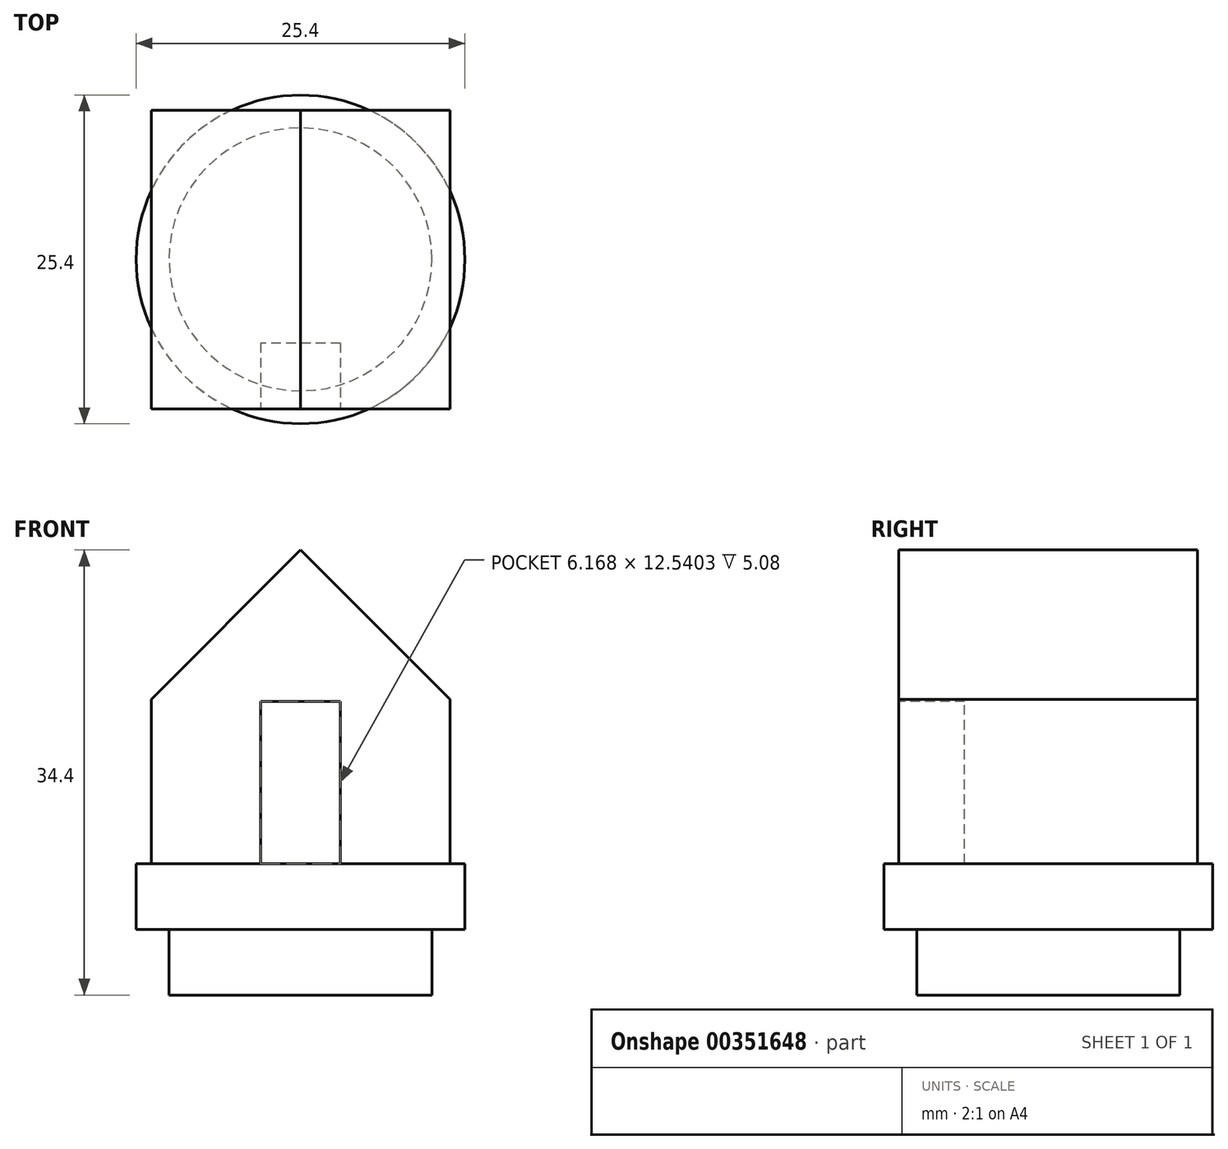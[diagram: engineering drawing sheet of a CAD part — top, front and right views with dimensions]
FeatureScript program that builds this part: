
annotation { "Feature Type Name" : "Feature", "Feature Type Description" : "" }
export const myFeature = defineFeature(function(context is Context, id is Id, definition is map)
    precondition{}
    {
        {
            var Q0;
            Q0=qCreatedBy(makeId("Top.planeOp"),FACE);
            var sketch = newSketch(context, id + "F0", { "sketchPlane" : qUnion([Q0])});
            skCircle(sketch, "E0", {"center": v(0, 0) * mm, "radius": 10.16 * mm});
            skSolve(sketch);
        }
        {
            var Q0;
            Q0=makeQuery(id+"F0.imprint","IMPRINT",FACE,{"disambiguationData":[TD([[makeQuery(id+"F0.imprint","IMPRINT",EDGE,{"derivedFrom":sQuery(id+"F0.wireOp",EDGE,"E0")}),1.0]])]});
            extrude(context, id + "F1", {"entities" : qUnion([Q0]), "depth" : 5.08 * mm});
        }
        {
            var Q0;
            Q0=makeQuery(id+"F1.opExtrude","CAP_FACE",FACE,{"disambiguationData":[OSD([sQuery(id+"F0.wireOp",EDGE,"E0")])],"isStart":false});
            var sketch = newSketch(context, id + "F2", { "sketchPlane" : qUnion([Q0])});
            skCircle(sketch, "E1", {"center": v(0, 0) * mm, "radius": 12.7 * mm});
            skSolve(sketch);
        }
        {
            var Q0;
            Q0=makeQuery(id+"F2.imprint","IMPRINT",FACE,{"disambiguationData":[TD([[makeQuery(id+"F2.imprint","IMPRINT",EDGE,{"derivedFrom":sQuery(id+"F2.wireOp",EDGE,"E1")}),1.0]])]});
            var Q1;
            Q1=makeQuery(id+"F2.imprint","IMPRINT",FACE,{"disambiguationData":[TD([[makeQuery(id+"F2.imprint","IMPRINT",EDGE,{"derivedFrom":makeQuery(id+"F1.opExtrude","CAP_EDGE",EDGE,{"disambiguationData":[OSD([sQuery(id+"F0.wireOp",EDGE,"E0")])],"isStart":false})}),1.0]])]});
            extrude(context, id + "F3", {"entities" : qUnion([Q0, Q1]), "operationType" : NewBodyOperationType.ADD, "depth" : 5.08 * mm});
        }
        {
            var Q0;
            Q0=makeQuery(id+"F3.opExtrude","CAP_FACE",FACE,{"disambiguationData":[OSD([sQuery(id+"F2.wireOp",EDGE,"E1")])],"isStart":false});
            var sketch = newSketch(context, id + "F4", { "sketchPlane" : qUnion([Q0])});
            skLineSegment(sketch, "E2", {"start": v(0, -11.54) * mm, "end": v(0, -12.7) * mm});
            skLineSegment(sketch, "E3", {"start": v(12.7, 0) * mm, "end": v(11.54, 0) * mm});
            skLineSegment(sketch, "E4", {"start": v(8.98, -8.98) * mm, "end": v(11.54, -11.54) * mm});
            skLineSegment(sketch, "E5.bottom", {"start": v(11.54, -11.54) * mm, "end": v(-11.54, -11.54) * mm});
            skLineSegment(sketch, "E5.top", {"start": v(11.54, 11.54) * mm, "end": v(-11.54, 11.54) * mm});
            skLineSegment(sketch, "E5.left", {"start": v(11.54, -11.54) * mm, "end": v(11.54, 11.54) * mm});
            skLineSegment(sketch, "E5.right", {"start": v(-11.54, -11.54) * mm, "end": v(-11.54, 11.54) * mm});
            skPoint(sketch, "E5.middle", {"position": v(0, 0) * mm});
            skSolve(sketch);
        }
        {
            var Q0;
            {var subQ0=sQuery(id+"F4.wireOp",EDGE,"E5.bottom");var subQ13=makeQuery(id+"F4.imprint","INTERSECT",VERTEX,{"derivedFrom":[sQuery(id+"F4.wireOp",EDGE,"E2"),subQ0]});Q0=makeQuery(id+"F4.imprint","IMPRINT",FACE,{"disambiguationData":[TD([[makeQuery(id+"F4.imprint","IMPRINT",EDGE,{"disambiguationData":[TD([[subQ13,1.0]])],"derivedFrom":subQ0}),-1.0]])]});}
            var Q1;
            {var subQ0=sQuery(id+"F4.wireOp",EDGE,"E5.right");var subQ1=sQuery(id+"F4.wireOp",EDGE,"E5.bottom");var subQ2=makeQuery(id+"F4.imprint","INTERSECT",VERTEX,{"derivedFrom":[subQ1,subQ0]});Q1=makeQuery(id+"F4.imprint","IMPRINT",FACE,{"disambiguationData":[TD([[makeQuery(id+"F4.imprint","IMPRINT",EDGE,{"disambiguationData":[TD([[subQ2,1.0]])],"derivedFrom":subQ1}),-1.0]])]});}
            var Q2;
            {var subQ0=sQuery(id+"F4.wireOp",EDGE,"E4");Q2=makeQuery(id+"F4.imprint","IMPRINT",FACE,{"disambiguationData":[TD([[makeQuery(id+"F4.imprint","IMPRINT",EDGE,{"derivedFrom":subQ0}),1.0]])]});}
            var Q3;
            {var subQ0=sQuery(id+"F4.wireOp",EDGE,"E4");Q3=makeQuery(id+"F4.imprint","IMPRINT",FACE,{"disambiguationData":[TD([[makeQuery(id+"F4.imprint","IMPRINT",EDGE,{"derivedFrom":subQ0}),-1.0]])]});}
            var Q4;
            {var subQ0=sQuery(id+"F4.wireOp",EDGE,"E5.right");var subQ1=sQuery(id+"F4.wireOp",EDGE,"E5.top");var subQ2=makeQuery(id+"F4.imprint","INTERSECT",VERTEX,{"derivedFrom":[subQ1,subQ0]});Q4=makeQuery(id+"F4.imprint","IMPRINT",FACE,{"disambiguationData":[TD([[makeQuery(id+"F4.imprint","IMPRINT",EDGE,{"disambiguationData":[TD([[subQ2,1.0]])],"derivedFrom":subQ1}),1.0]])]});}
            var Q5;
            {var subQ0=sQuery(id+"F4.wireOp",EDGE,"E5.left");var subQ1=sQuery(id+"F4.wireOp",EDGE,"E5.top");var subQ2=makeQuery(id+"F4.imprint","INTERSECT",VERTEX,{"derivedFrom":[subQ1,subQ0]});Q5=makeQuery(id+"F4.imprint","IMPRINT",FACE,{"disambiguationData":[TD([[makeQuery(id+"F4.imprint","IMPRINT",EDGE,{"disambiguationData":[TD([[subQ2,-1.0]])],"derivedFrom":subQ1}),1.0]])]});}
            extrude(context, id + "F5", {"entities" : qUnion([Q0, Q1, Q2, Q3, Q4, Q5]), "operationType" : NewBodyOperationType.ADD, "depth" : 25.4 * mm});
        }
        {
            var Q0;
            Q0=makeQuery(id+"F5.opExtrude","CAP_EDGE",EDGE,{"disambiguationData":[OSD([sQuery(id+"F4.wireOp",EDGE,"E5.left")])],"isStart":false});
            var Q1;
            Q1=makeQuery(id+"F5.opExtrude","CAP_EDGE",EDGE,{"disambiguationData":[OSD([sQuery(id+"F4.wireOp",EDGE,"E5.right")])],"isStart":false});
            chamfer(context, id + "F6", {"entities" : qUnion([Q0, Q1]), "width" : 12.7 * mm, "tangentPropagation" : true});
        }
        {
            var Q0;
            Q0=makeQuery(id+"F5.opExtrude","SWEPT_FACE",FACE,{"disambiguationData":[OSD([sQuery(id+"F4.wireOp",EDGE,"E5.bottom")])]});
            var sketch = newSketch(context, id + "F7", { "sketchPlane" : qUnion([Q0])});
            skPoint(sketch, "E6", {"position": v(0, 18.3) * mm});
            skPoint(sketch, "E7", {"position": v(0, 13.75) * mm});
            skPoint(sketch, "E8", {"position": v(0, 16.43) * mm});
            skLineSegment(sketch, "E9.bottom", {"start": v(3.08, 10.16) * mm, "end": v(-3.08, 10.16) * mm});
            skLineSegment(sketch, "E9.top", {"start": v(3.08, 22.7) * mm, "end": v(-3.08, 22.7) * mm});
            skLineSegment(sketch, "E9.left", {"start": v(3.08, 10.16) * mm, "end": v(3.08, 22.7) * mm});
            skLineSegment(sketch, "E9.right", {"start": v(-3.08, 10.16) * mm, "end": v(-3.08, 22.7) * mm});
            skSolve(sketch);
        }
        {
            var Q0;
            Q0 = qSketchRegion(id + "F7", true);
            extrude(context, id + "F8", {"entities" : qUnion([Q0]), "operationType" : NewBodyOperationType.REMOVE, "oppositeDirection" : true, "depth" : 5.08 * mm});
        }
    });
